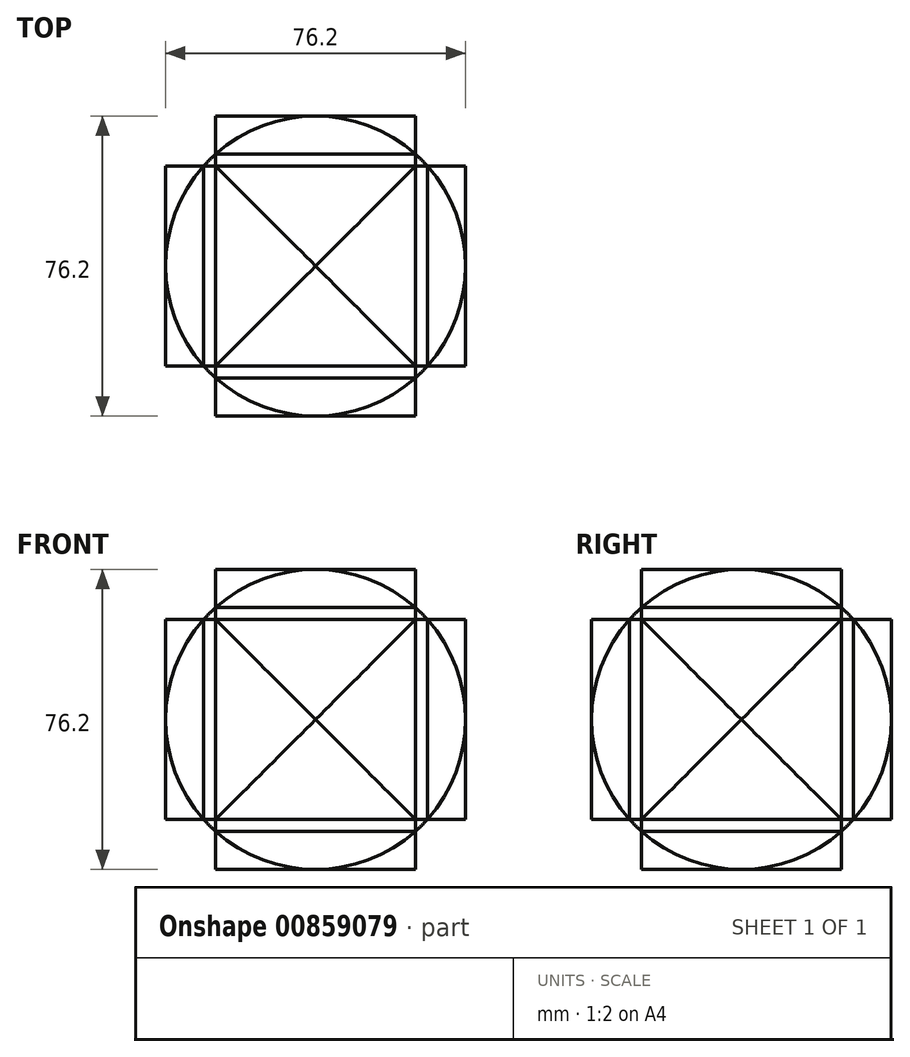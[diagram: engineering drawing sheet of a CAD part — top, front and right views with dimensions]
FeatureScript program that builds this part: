
annotation { "Feature Type Name" : "Feature", "Feature Type Description" : "" }
export const myFeature = defineFeature(function(context is Context, id is Id, definition is map)
    precondition{}
    {
        {
            var Q0;
            Q0=qCreatedBy(makeId("Front.planeOp"),FACE);
            var sketch = newSketch(context, id + "F0", { "sketchPlane" : qUnion([Q0])});
            skCircle(sketch, "E0", {"center": v(0, 0) * mm, "radius": 38.1 * mm});
            skSolve(sketch);
        }
        {
            var Q0;
            Q0=qSketchRegion(id+"F0",true);
            extrude(context, id + "F1", {"entities" : qUnion([Q0]), "depth" : 25.4 * mm, "offsetDistance" : 25.4 * mm});
        }
        {
            var Q0;
            Q0=qCreatedBy(makeId("Top.planeOp"),FACE);
            var sketch = newSketch(context, id + "F2", { "sketchPlane" : qUnion([Q0])});
            skCircle(sketch, "E1", {"center": v(0, 0) * mm, "radius": 38.1 * mm});
            skSolve(sketch);
        }
        {
            var Q0;
            Q0=qSketchRegion(id+"F2",true);
            extrude(context, id + "F3", {"entities" : qUnion([Q0]), "operationType" : NewBodyOperationType.ADD, "depth" : 25.4 * mm, "offsetDistance" : 25.4 * mm});
        }
        {
            var Q0;
            Q0=qCreatedBy(makeId("Right.planeOp"),FACE);
            var sketch = newSketch(context, id + "F4", { "sketchPlane" : qUnion([Q0])});
            skCircle(sketch, "E2", {"center": v(0, 0) * mm, "radius": 38.1 * mm});
            skSolve(sketch);
        }
        {
            var Q0;
            Q0=qSketchRegion(id+"F4",true);
            extrude(context, id + "F5", {"entities" : qUnion([Q0]), "operationType" : NewBodyOperationType.ADD, "depth" : 25.4 * mm, "offsetDistance" : 25.4 * mm});
        }
        {
            var Q0;
            Q0=qCreatedBy(makeId("Top.planeOp"),FACE);
            var sketch = newSketch(context, id + "F6", { "sketchPlane" : qUnion([Q0])});
            skCircle(sketch, "E3", {"center": v(0, 0) * mm, "radius": 38.1 * mm});
            skSolve(sketch);
        }
        {
            var Q0;
            Q0=qSketchRegion(id+"F6",true);
            extrude(context, id + "F7", {"entities" : qUnion([Q0]), "operationType" : NewBodyOperationType.ADD, "depth" : -25.4 * mm, "offsetDistance" : 25.4 * mm});
        }
        {
            var Q0;
            Q0=qCreatedBy(makeId("Front.planeOp"),FACE);
            var sketch = newSketch(context, id + "F8", { "sketchPlane" : qUnion([Q0])});
            skCircle(sketch, "E4", {"center": v(0, 0) * mm, "radius": 38.1 * mm});
            skSolve(sketch);
        }
        {
            var Q0;
            Q0=qSketchRegion(id+"F8",true);
            extrude(context, id + "F9", {"entities" : qUnion([Q0]), "operationType" : NewBodyOperationType.ADD, "depth" : -25.4 * mm, "offsetDistance" : 25.4 * mm});
        }
        {
            var Q0;
            Q0=qCreatedBy(makeId("Right.planeOp"),FACE);
            var sketch = newSketch(context, id + "F10", { "sketchPlane" : qUnion([Q0])});
            skCircle(sketch, "E5", {"center": v(0, 0) * mm, "radius": 38.1 * mm});
            skSolve(sketch);
        }
        {
            var Q0;
            Q0=qSketchRegion(id+"F10",true);
            extrude(context, id + "F11", {"entities" : qUnion([Q0]), "operationType" : NewBodyOperationType.ADD, "depth" : -25.4 * mm, "offsetDistance" : 25.4 * mm});
        }
    });
